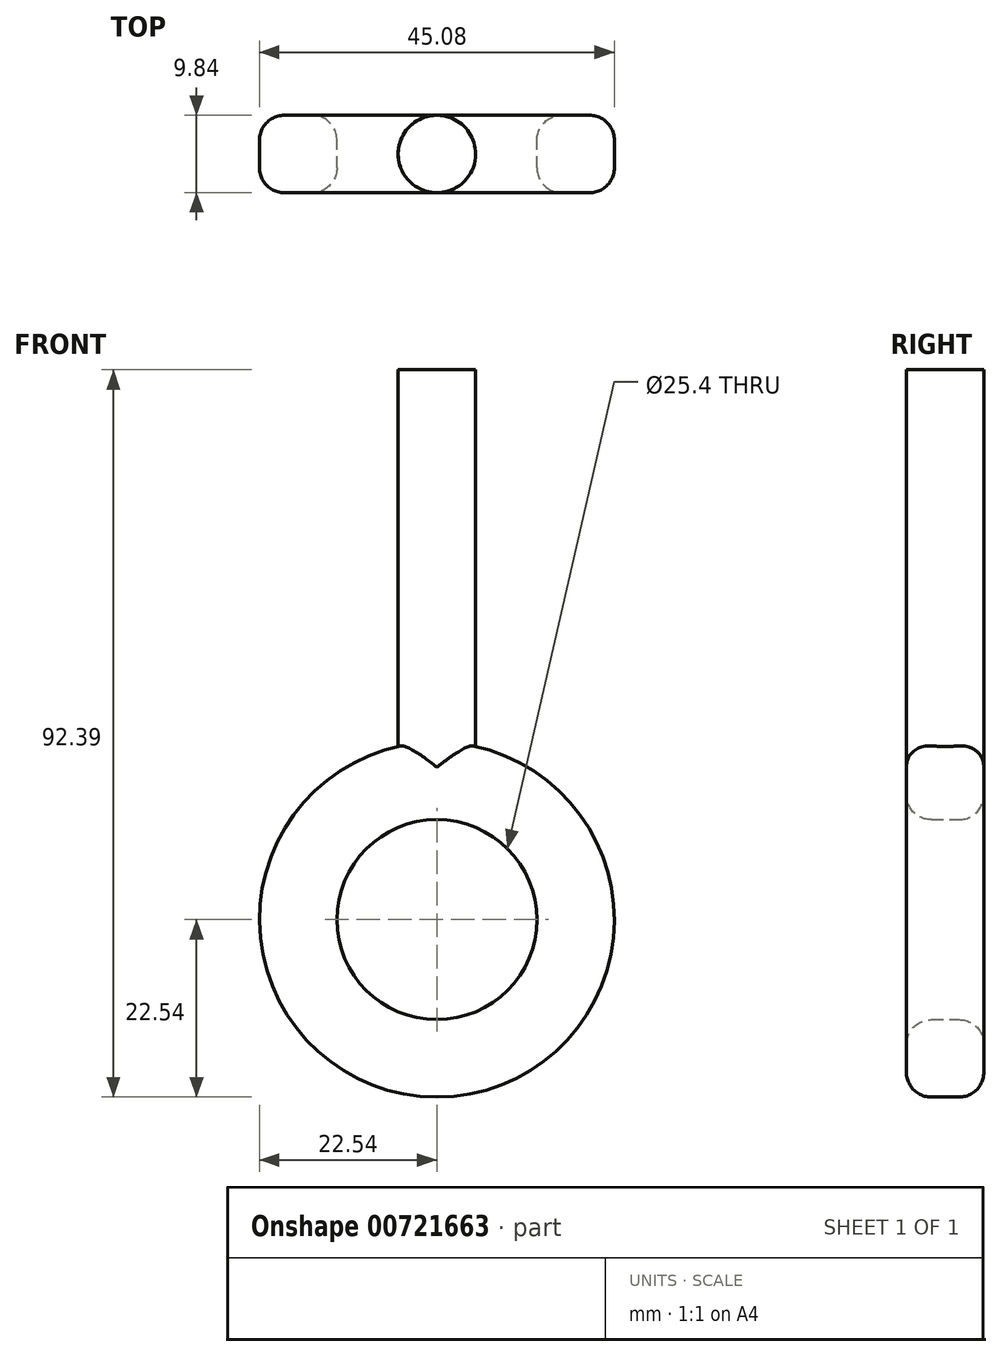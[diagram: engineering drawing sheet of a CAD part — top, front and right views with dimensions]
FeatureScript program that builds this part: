
annotation { "Feature Type Name" : "Feature", "Feature Type Description" : "" }
export const myFeature = defineFeature(function(context is Context, id is Id, definition is map)
    precondition{}
    {
        {
            var Q0;
            Q0=qCreatedBy(makeId("Front.planeOp"),FACE);
            var sketch = newSketch(context, id + "F0", { "sketchPlane" : qUnion([Q0])});
            skCircle(sketch, "E0", {"center": v(0, 0) * mm, "radius": 12.7 * mm});
            skCircle(sketch, "E1.0", {"center": v(0, 0) * mm, "radius": 22.54 * mm});
            skSolve(sketch);
        }
        {
            var Q0;
            Q0 = qSketchRegion(id + "F0", true);
            extrude(context, id + "F1", {"entities" : qUnion([Q0]), "depth" : 9.84 * mm, "offsetDistance" : 25.4 * mm});
        }
        {
            var Q0;
            Q0=makeQuery(id+"F1.opExtrude","CAP_EDGE",EDGE,{"disambiguationData":[OSD([sQuery(id+"F0.wireOp",EDGE,"E1.0")])],"isStart":false});
            var Q1;
            Q1=makeQuery(id+"F1.opExtrude","CAP_EDGE",EDGE,{"disambiguationData":[OSD([sQuery(id+"F0.wireOp",EDGE,"E1.0")])],"isStart":true});
            fillet(context, id + "F2", {"entities" : qUnion([Q0, Q1]), "radius" : 3.17 * mm, "tangentPropagation" : true, "allowEdgeOverflow" : false});
        }
        {
            var Q0;
            Q0=makeQuery(id+"F1.opExtrude","CAP_EDGE",EDGE,{"disambiguationData":[OSD([sQuery(id+"F0.wireOp",EDGE,"E0")])],"isStart":false});
            var Q1;
            Q1=makeQuery(id+"F1.opExtrude","CAP_EDGE",EDGE,{"disambiguationData":[OSD([sQuery(id+"F0.wireOp",EDGE,"E0")])],"isStart":true});
            fillet(context, id + "F3", {"entities" : qUnion([Q0, Q1]), "radius" : 3.17 * mm, "tangentPropagation" : true, "allowEdgeOverflow" : false});
        }
        {
            var Q0;
            Q0=qCreatedBy(makeId("Top.planeOp"),FACE);
            cPlane(context, id + "F4", {"entities" : qUnion([Q0]), "cplaneType" : CPlaneType.OFFSET, "offset" : 19.05 * mm, "width" : 152.4 * mm, "height" : 152.4 * mm});
        }
        {
            var Q0;
            Q0=qCreatedBy(id+"F4.planeOp",FACE);
            var sketch = newSketch(context, id + "F5", { "sketchPlane" : qUnion([Q0])});
            skCircle(sketch, "E2", {"center": v(0, -4.92) * mm, "radius": 4.92 * mm});
            skSolve(sketch);
        }
        {
            var Q0;
            Q0 = qSketchRegion(id + "F5", true);
            extrude(context, id + "F6", {"entities" : qUnion([Q0]), "operationType" : NewBodyOperationType.ADD, "depth" : 50.8 * mm, "offsetDistance" : 25.4 * mm, "hasSecondDirection" : true, "secondDirectionOppositeDirection" : true, "secondDirectionDepth" : 3.17 * mm});
        }
    });
